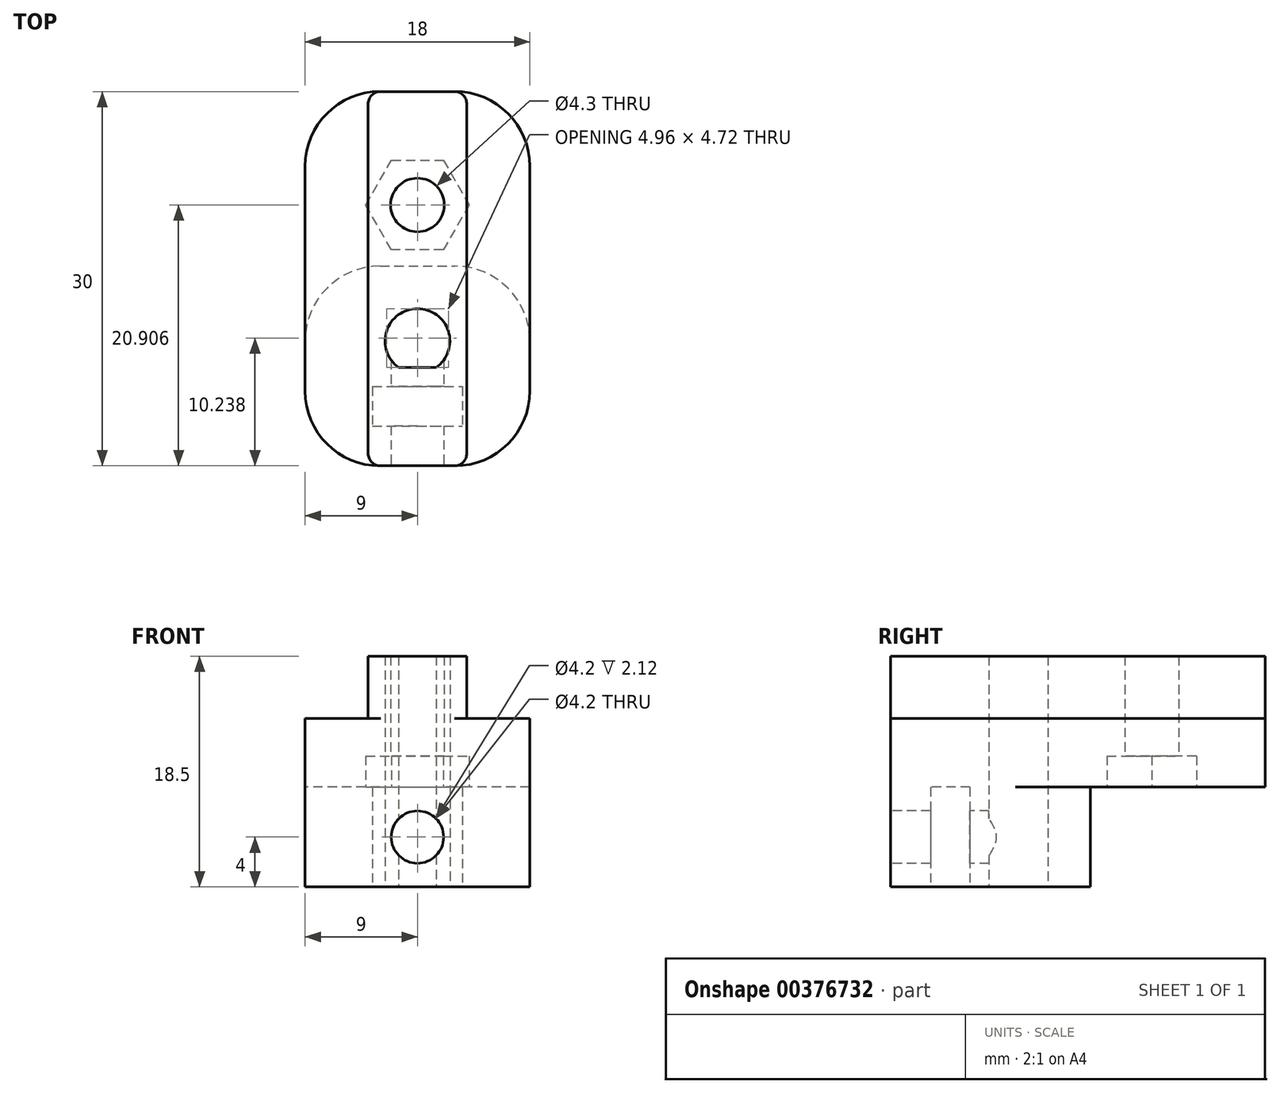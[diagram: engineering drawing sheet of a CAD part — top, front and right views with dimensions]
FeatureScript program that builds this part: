
annotation { "Feature Type Name" : "Feature", "Feature Type Description" : "" }
export const myFeature = defineFeature(function(context is Context, id is Id, definition is map)
    precondition{}
    {
        {
            var Q0;
            Q0=qCreatedBy(makeId("Top.planeOp"),FACE);
            var sketch = newSketch(context, id + "F0", { "sketchPlane" : qUnion([Q0])});
            skCircle(sketch, "E0", {"center": v(0, 0) * mm, "radius": 2.6 * mm});
            skLineSegment(sketch, "E1.bottom", {"start": v(-9, 6) * mm, "end": v(9, 6) * mm});
            skLineSegment(sketch, "E1.top", {"start": v(-9, -10) * mm, "end": v(9, -10) * mm});
            skLineSegment(sketch, "E1.left", {"start": v(-9, 6) * mm, "end": v(-9, -10) * mm});
            skLineSegment(sketch, "E1.right", {"start": v(9, 6) * mm, "end": v(9, -10) * mm});
            skLineSegment(sketch, "E2.bottom", {"start": v(-3.6, -3.65) * mm, "end": v(3.6, -3.65) * mm});
            skLineSegment(sketch, "E2.top", {"start": v(-3.6, -6.8) * mm, "end": v(3.6, -6.8) * mm});
            skLineSegment(sketch, "E2.left", {"start": v(-3.6, -3.65) * mm, "end": v(-3.6, -6.8) * mm});
            skLineSegment(sketch, "E2.right", {"start": v(3.6, -3.65) * mm, "end": v(3.6, -6.8) * mm});
            skLineSegment(sketch, "E3", {"start": v(-1.5, -2.12) * mm, "end": v(1.5, -2.12) * mm});
            skSolve(sketch);
        }
        {
            var Q0;
            Q0=makeQuery(id+"F0.imprint","IMPRINT",FACE,{"disambiguationData":[TD([[makeQuery(id+"F0.imprint","IMPRINT",EDGE,{"derivedFrom":sQuery(id+"F0.wireOp",EDGE,"E1.bottom")}),-1.0]])]});
            var Q1;
            {var subQ0=sQuery(id+"F0.wireOp",EDGE,"E3");Q1=makeQuery(id+"F0.imprint","IMPRINT",FACE,{"disambiguationData":[TD([[makeQuery(id+"F0.imprint","IMPRINT",EDGE,{"derivedFrom":subQ0}),-1.0]])]});}
            extrude(context, id + "F1", {"entities" : qUnion([Q0, Q1]), "depth" : 8 * mm});
        }
        {
            var Q0;
            Q0=makeQuery(id+"F1.opExtrude","SWEPT_EDGE",EDGE,{"disambiguationData":[OSD([sQuery(id+"F0.wireOp",EDGE,"E1.top"),sQuery(id+"F0.wireOp",EDGE,"E1.right")])]});
            var Q1;
            Q1=makeQuery(id+"F1.opExtrude","SWEPT_EDGE",EDGE,{"disambiguationData":[OSD([sQuery(id+"F0.wireOp",EDGE,"E1.top"),sQuery(id+"F0.wireOp",EDGE,"E1.left")])]});
            var Q2;
            Q2=makeQuery(id+"F1.opExtrude","SWEPT_EDGE",EDGE,{"disambiguationData":[OSD([sQuery(id+"F0.wireOp",EDGE,"E1.bottom"),sQuery(id+"F0.wireOp",EDGE,"E1.right")])]});
            var Q3;
            Q3=makeQuery(id+"F1.opExtrude","SWEPT_EDGE",EDGE,{"disambiguationData":[OSD([sQuery(id+"F0.wireOp",EDGE,"E1.bottom"),sQuery(id+"F0.wireOp",EDGE,"E1.left")])]});
            fillet(context, id + "F2", {"entities" : qUnion([Q0, Q1, Q2, Q3]), "radius" : 6 * mm, "tangentPropagation" : true, "allowEdgeOverflow" : false});
        }
        {
            var Q0;
            Q0=makeQuery(id+"F1.opExtrude","SWEPT_FACE",FACE,{"disambiguationData":[OSD([sQuery(id+"F0.wireOp",EDGE,"E1.top")])]});
            cPlane(context, id + "F3", {"entities" : qUnion([Q0]), "cplaneType" : CPlaneType.OFFSET, "offset" : 0 * mm, "width" : 150 * mm, "height" : 150 * mm});
        }
        {
            var Q0;
            Q0=qCreatedBy(id+"F3.planeOp",FACE);
            var sketch = newSketch(context, id + "F4", { "sketchPlane" : qUnion([Q0])});
            skCircle(sketch, "E4", {"center": v(0, 4) * mm, "radius": 2.1 * mm});
            skSolve(sketch);
        }
        {
            var Q0;
            Q0=makeQuery(id+"F4.imprint","IMPRINT",FACE,{"disambiguationData":[TD([[makeQuery(id+"F4.imprint","IMPRINT",EDGE,{"derivedFrom":sQuery(id+"F4.wireOp",EDGE,"E4")}),1.0]])]});
            extrude(context, id + "F5", {"entities" : qUnion([Q0]), "operationType" : NewBodyOperationType.REMOVE, "oppositeDirection" : true, "depth" : 10 * mm});
        }
        {
            var Q0;
            Q0=qCreatedBy(makeId("Top.planeOp"),FACE);
            cPlane(context, id + "F6", {"entities" : qUnion([Q0]), "cplaneType" : CPlaneType.OFFSET, "offset" : 8 * mm, "width" : 150 * mm, "height" : 150 * mm});
        }
        {
            var Q0;
            Q0=qCreatedBy(id+"F6.planeOp",FACE);
            var sketch = newSketch(context, id + "F7", { "sketchPlane" : qUnion([Q0])});
            skLineSegment(sketch, "E5.0", {"start": v(-9, 0) * mm, "end": v(-9, -4) * mm});
            skLineSegment(sketch, "E6.0", {"start": v(9, 0) * mm, "end": v(9, -4) * mm});
            skLineSegment(sketch, "E7.0", {"start": v(-3, -10) * mm, "end": v(3, -10) * mm});
            skLineSegment(sketch, "E8.bottom", {"start": v(-9, -10) * mm, "end": v(9, -10) * mm});
            skLineSegment(sketch, "E8.top", {"start": v(-9, 20) * mm, "end": v(9, 20) * mm});
            skLineSegment(sketch, "E8.left", {"start": v(-9, -10) * mm, "end": v(-9, 20) * mm});
            skLineSegment(sketch, "E8.right", {"start": v(9, -10) * mm, "end": v(9, 20) * mm});
            skCircle(sketch, "E9", {"center": v(0, 10.9) * mm, "radius": 4.15 * mm});
            skCircle(sketch, "E10.cCircle", {"center": v(0, 10.9) * mm, "radius": 4.15 * mm, "construction": true});
            skLineSegment(sketch, "E10.0", {"start": v(-4.15, 10.9) * mm, "end": v(-2.07, 14.5) * mm});
            skLineSegment(sketch, "E10.1", {"start": v(-2.07, 14.5) * mm, "end": v(2.07, 14.5) * mm});
            skLineSegment(sketch, "E10.2", {"start": v(2.07, 14.5) * mm, "end": v(4.15, 10.9) * mm});
            skLineSegment(sketch, "E10.3", {"start": v(4.15, 10.9) * mm, "end": v(2.07, 7.31) * mm});
            skLineSegment(sketch, "E10.4", {"start": v(2.07, 7.31) * mm, "end": v(-2.07, 7.31) * mm});
            skLineSegment(sketch, "E10.5", {"start": v(-2.07, 7.31) * mm, "end": v(-4.15, 10.9) * mm});
            skCircle(sketch, "E11", {"center": v(0, 10.9) * mm, "radius": 2.15 * mm});
            skArc(sketch, "E12.0", {"start": v(1.5, -2.12) * mm, "mid": v(0, 2.6) * mm, "end": v(-1.5, -2.12) * mm});
            skLineSegment(sketch, "E13.0", {"start": v(-1.5, -2.12) * mm, "end": v(1.5, -2.12) * mm});
            skSolve(sketch);
        }
        {
            var Q0;
            {var subQ3=sQuery(id+"F7.wireOp",EDGE,"E8.top");Q0=makeQuery(id+"F7.imprint","IMPRINT",FACE,{"disambiguationData":[TD([[makeQuery(id+"F7.imprint","IMPRINT",EDGE,{"derivedFrom":subQ3}),-1.0]])]});}
            var Q1;
            {var subQ0=sQuery(id+"F7.wireOp",EDGE,"E10.5");Q1=makeQuery(id+"F7.imprint","IMPRINT",FACE,{"disambiguationData":[TD([[makeQuery(id+"F7.imprint","IMPRINT",EDGE,{"derivedFrom":subQ0}),1.0]])]});}
            var Q2;
            {var subQ0=sQuery(id+"F7.wireOp",EDGE,"E10.0");Q2=makeQuery(id+"F7.imprint","IMPRINT",FACE,{"disambiguationData":[TD([[makeQuery(id+"F7.imprint","IMPRINT",EDGE,{"derivedFrom":subQ0}),1.0]])]});}
            var Q3;
            {var subQ0=sQuery(id+"F7.wireOp",EDGE,"E10.1");Q3=makeQuery(id+"F7.imprint","IMPRINT",FACE,{"disambiguationData":[TD([[makeQuery(id+"F7.imprint","IMPRINT",EDGE,{"derivedFrom":subQ0}),1.0]])]});}
            var Q4;
            {var subQ0=sQuery(id+"F7.wireOp",EDGE,"E10.2");Q4=makeQuery(id+"F7.imprint","IMPRINT",FACE,{"disambiguationData":[TD([[makeQuery(id+"F7.imprint","IMPRINT",EDGE,{"derivedFrom":subQ0}),1.0]])]});}
            var Q5;
            {var subQ0=sQuery(id+"F7.wireOp",EDGE,"E10.3");Q5=makeQuery(id+"F7.imprint","IMPRINT",FACE,{"disambiguationData":[TD([[makeQuery(id+"F7.imprint","IMPRINT",EDGE,{"derivedFrom":subQ0}),1.0]])]});}
            var Q6;
            {var subQ0=sQuery(id+"F7.wireOp",EDGE,"E10.4");Q6=makeQuery(id+"F7.imprint","IMPRINT",FACE,{"disambiguationData":[TD([[makeQuery(id+"F7.imprint","IMPRINT",EDGE,{"derivedFrom":subQ0}),1.0]])]});}
            var Q7;
            Q7=makeQuery(id+"F7.imprint","IMPRINT",FACE,{"disambiguationData":[TD([[makeQuery(id+"F7.imprint","IMPRINT",EDGE,{"derivedFrom":sQuery(id+"F7.wireOp",EDGE,"E10.0")}),-1.0]])]});
            extrude(context, id + "F8", {"entities" : qUnion([Q0, Q1, Q2, Q3, Q4, Q5, Q6, Q7]), "operationType" : NewBodyOperationType.ADD, "depth" : 5.5 * mm});
        }
        {
            var Q0;
            Q0=makeQuery(id+"F7.imprint","IMPRINT",FACE,{"disambiguationData":[TD([[makeQuery(id+"F7.imprint","IMPRINT",EDGE,{"derivedFrom":sQuery(id+"F7.wireOp",EDGE,"E10.0")}),-1.0]])]});
            extrude(context, id + "F9", {"entities" : qUnion([Q0]), "operationType" : NewBodyOperationType.REMOVE, "depth" : 2.5 * mm});
        }
        {
            var Q0;
            Q0=makeQuery(id+"F8.opExtrude","SWEPT_EDGE",EDGE,{"disambiguationData":[OSD([sQuery(id+"F7.wireOp",EDGE,"E8.bottom"),sQuery(id+"F7.wireOp",EDGE,"E8.left")])]});
            var Q1;
            Q1=makeQuery(id+"F8.opExtrude","SWEPT_EDGE",EDGE,{"disambiguationData":[OSD([sQuery(id+"F7.wireOp",EDGE,"E8.bottom"),sQuery(id+"F7.wireOp",EDGE,"E8.right")])]});
            var Q2;
            Q2=makeQuery(id+"F8.opExtrude","SWEPT_EDGE",EDGE,{"disambiguationData":[OSD([sQuery(id+"F7.wireOp",EDGE,"E8.top"),sQuery(id+"F7.wireOp",EDGE,"E8.right")])]});
            var Q3;
            Q3=makeQuery(id+"F8.opExtrude","SWEPT_EDGE",EDGE,{"disambiguationData":[OSD([sQuery(id+"F7.wireOp",EDGE,"E8.top"),sQuery(id+"F7.wireOp",EDGE,"E8.left")])]});
            fillet(context, id + "F10", {"entities" : qUnion([Q0, Q1, Q2, Q3]), "radius" : 6 * mm, "tangentPropagation" : true, "allowEdgeOverflow" : false});
        }
        {
            var Q0;
            Q0=makeQuery(id+"F8.opExtrude","CAP_FACE",FACE,{"disambiguationData":[OSD([sQuery(id+"F7.wireOp",EDGE,"E8.bottom"),sQuery(id+"F7.wireOp",EDGE,"E8.top"),sQuery(id+"F7.wireOp",EDGE,"E8.left"),sQuery(id+"F7.wireOp",EDGE,"E8.right"),sQuery(id+"F7.wireOp",EDGE,"E11")])],"isStart":false});
            cPlane(context, id + "F11", {"entities" : qUnion([Q0]), "cplaneType" : CPlaneType.OFFSET, "offset" : 0 * mm, "width" : 150 * mm, "height" : 150 * mm});
        }
        {
            var Q0;
            Q0=qCreatedBy(id+"F11.planeOp",FACE);
            var sketch = newSketch(context, id + "F12", { "sketchPlane" : qUnion([Q0])});
            skCircle(sketch, "E14.0", {"center": v(0, 10.9) * mm, "radius": 2.15 * mm});
            skLineSegment(sketch, "E15.0", {"start": v(-9, -10) * mm, "end": v(-9, 20) * mm});
            skLineSegment(sketch, "E16.0", {"start": v(-9, 20) * mm, "end": v(9, 20) * mm});
            skLineSegment(sketch, "E17.0", {"start": v(9, -10) * mm, "end": v(9, 20) * mm});
            skLineSegment(sketch, "E18.0", {"start": v(-9, -10) * mm, "end": v(9, -10) * mm});
            skLineSegment(sketch, "E19.bottom", {"start": v(-3.95, 20) * mm, "end": v(3.95, 20) * mm});
            skLineSegment(sketch, "E19.top", {"start": v(-3.95, -10) * mm, "end": v(3.95, -10) * mm});
            skLineSegment(sketch, "E19.left", {"start": v(-3.95, 20) * mm, "end": v(-3.95, -10) * mm});
            skLineSegment(sketch, "E19.right", {"start": v(3.95, 20) * mm, "end": v(3.95, -10) * mm});
            skArc(sketch, "E20.0", {"start": v(-3, 20) * mm, "mid": v(-7.24, 18.24) * mm, "end": v(-9, 14) * mm});
            skArc(sketch, "E21.0", {"start": v(9, 14) * mm, "mid": v(7.24, 18.24) * mm, "end": v(3, 20) * mm});
            skArc(sketch, "E22.0", {"start": v(3, -10) * mm, "mid": v(7.24, -8.24) * mm, "end": v(9, -4) * mm});
            skArc(sketch, "E23.0", {"start": v(-9, -4) * mm, "mid": v(-7.24, -8.24) * mm, "end": v(-3, -10) * mm});
            skLineSegment(sketch, "E24.0", {"start": v(-1.5, -2.12) * mm, "end": v(1.5, -2.12) * mm});
            skPoint(sketch, "E25.0.end.orphan", {"position": v(-1.5, -2.12) * mm});
            skPoint(sketch, "E25.0.start.orphan", {"position": v(1.5, -2.12) * mm});
            skArc(sketch, "E26.0", {"start": v(1.5, -2.12) * mm, "mid": v(0, 2.6) * mm, "end": v(-1.5, -2.12) * mm});
            skSolve(sketch);
        }
        {
            var Q0;
            Q0=makeQuery(id+"F12.imprint","IMPRINT",FACE,{"disambiguationData":[TD([[makeQuery(id+"F12.imprint","IMPRINT",EDGE,{"derivedFrom":sQuery(id+"F12.wireOp",EDGE,"E14.0")}),-1.0]])]});
            extrude(context, id + "F13", {"entities" : qUnion([Q0]), "operationType" : NewBodyOperationType.ADD, "depth" : 5 * mm});
        }
        {
            var Q0;
            Q0=makeQuery(id+"F13.opExtrude","SWEPT_EDGE",EDGE,{"disambiguationData":[OSD([sQuery(id+"F12.wireOp",EDGE,"E19.right"),sQuery(id+"F12.wireOp",EDGE,"E22.0")])]});
            var Q1;
            Q1=makeQuery(id+"F13.opExtrude","SWEPT_EDGE",EDGE,{"disambiguationData":[OSD([sQuery(id+"F12.wireOp",EDGE,"E19.left"),sQuery(id+"F12.wireOp",EDGE,"E23.0")])]});
            var Q2;
            Q2=makeQuery(id+"F13.opExtrude","SWEPT_EDGE",EDGE,{"disambiguationData":[OSD([sQuery(id+"F12.wireOp",EDGE,"E19.right"),sQuery(id+"F12.wireOp",EDGE,"E21.0")])]});
            var Q3;
            Q3=makeQuery(id+"F13.opExtrude","SWEPT_EDGE",EDGE,{"disambiguationData":[OSD([sQuery(id+"F12.wireOp",EDGE,"E19.left"),sQuery(id+"F12.wireOp",EDGE,"E20.0")])]});
            fillet(context, id + "F14", {"entities" : qUnion([Q0, Q1, Q2, Q3]), "radius" : 1 * mm, "tangentPropagation" : true, "allowEdgeOverflow" : false});
        }
    });
